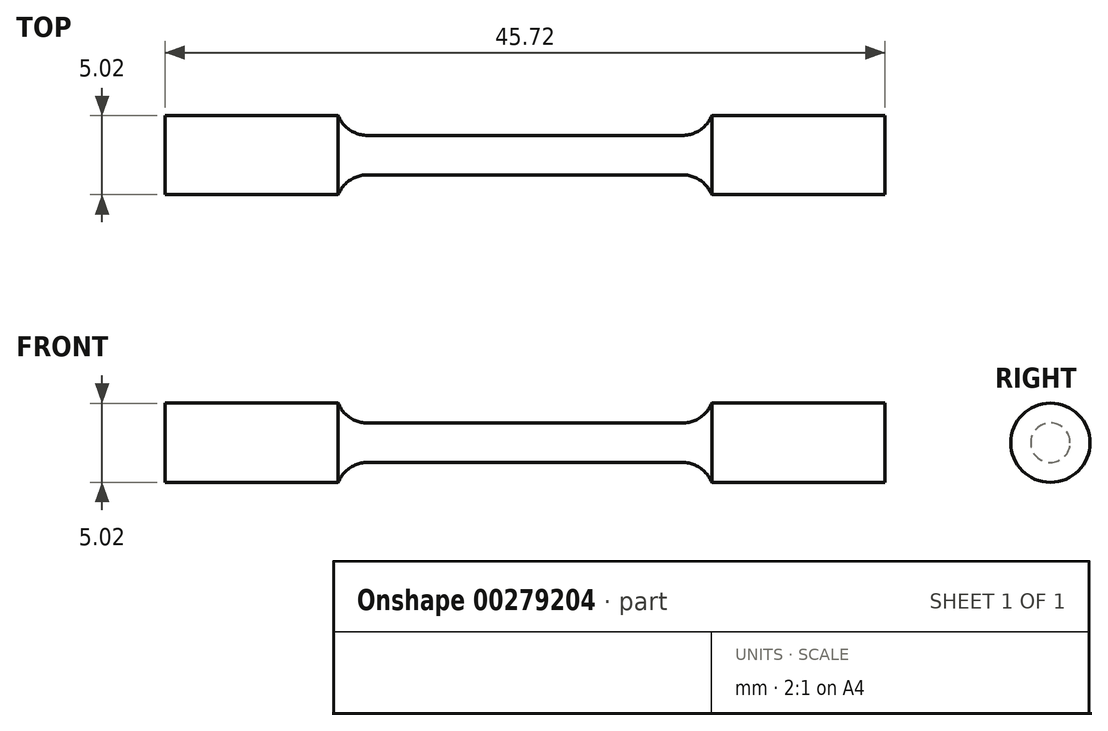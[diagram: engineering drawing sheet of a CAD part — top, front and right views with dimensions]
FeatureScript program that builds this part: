
annotation { "Feature Type Name" : "Feature", "Feature Type Description" : "" }
export const myFeature = defineFeature(function(context is Context, id is Id, definition is map)
    precondition{}
    {
        {
            var Q0;
            Q0=qCreatedBy(makeId("Front.planeOp"),FACE);
            var sketch = newSketch(context, id + "F0", { "sketchPlane" : qUnion([Q0])});
            skLineSegment(sketch, "E0", {"start": v(0, 1.25) * mm, "end": v(10, 1.25) * mm});
            skArc(sketch, "E1", {"start": v(10, 1.25) * mm, "mid": v(11.12, 1.6) * mm, "end": v(11.86, 2.51) * mm});
            skLineSegment(sketch, "E2", {"start": v(11.86, 2.51) * mm, "end": v(22.86, 2.51) * mm});
            skLineSegment(sketch, "E3", {"start": v(22.86, 0) * mm, "end": v(22.86, 2.51) * mm});
            skLineSegment(sketch, "E4.MirrorCS", {"start": v(0, 1.25) * mm, "end": v(-10, 1.25) * mm});
            skLineSegment(sketch, "E5.MirrorCS", {"start": v(-22.86, 0) * mm, "end": v(-22.86, 2.51) * mm});
            skLineSegment(sketch, "E6.MirrorCS", {"start": v(-11.86, 2.51) * mm, "end": v(-22.86, 2.51) * mm});
            skArc(sketch, "E7.MirrorCS", {"start": v(-10, 1.25) * mm, "mid": v(-11.12, 1.6) * mm, "end": v(-11.86, 2.51) * mm});
            skLineSegment(sketch, "E8", {"start": v(-22.86, 0) * mm, "end": v(22.86, 0) * mm});
            skSolve(sketch);
        }
        {
            var Q0;
            Q0=makeQuery(id+"F0.imprint","IMPRINT",FACE,{"disambiguationData":[TD([[makeQuery(id+"F0.imprint","IMPRINT",EDGE,{"derivedFrom":sQuery(id+"F0.wireOp",EDGE,"E0")}),-1.0]])]});
            var Q1;
            Q1=sQuery(id+"F0.wireOp",EDGE,"E8");
            revolve(context, id + "F1", {"entities" : qUnion([Q0]), "axis" : qUnion([Q1]), "revolveType" : RevolveType.FULL});
        }
    });
